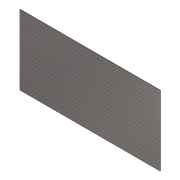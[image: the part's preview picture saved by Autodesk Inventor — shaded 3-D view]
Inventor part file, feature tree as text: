
AUTODESK INVENTOR PART (.ipt)
format: ipt  version: 2012 (Build 160160000, 160)  size: 94,720 bytes
history: native  units: in
note: dims shown in document units (in); Inventor stores cm internally (conversion verified against a paired STEP export)
features: extrude x1, plane x1, sketch x1
ambient origin geometry x8: Origin, YZ Plane, XZ Plane, XY Plane, X Axis, Y Axis, Z Axis, Center Point
bodies: Solid1 (feature_tree)
feature tree (3):
  extrude  "Extrusion1"  Depth=36.0in
  plane  "Work Plane1"
  sketch  "Sketch1"  dims[d0=72.0in d1=36.0in d2=0.1875in d3=0.0in d38=0.05in]
